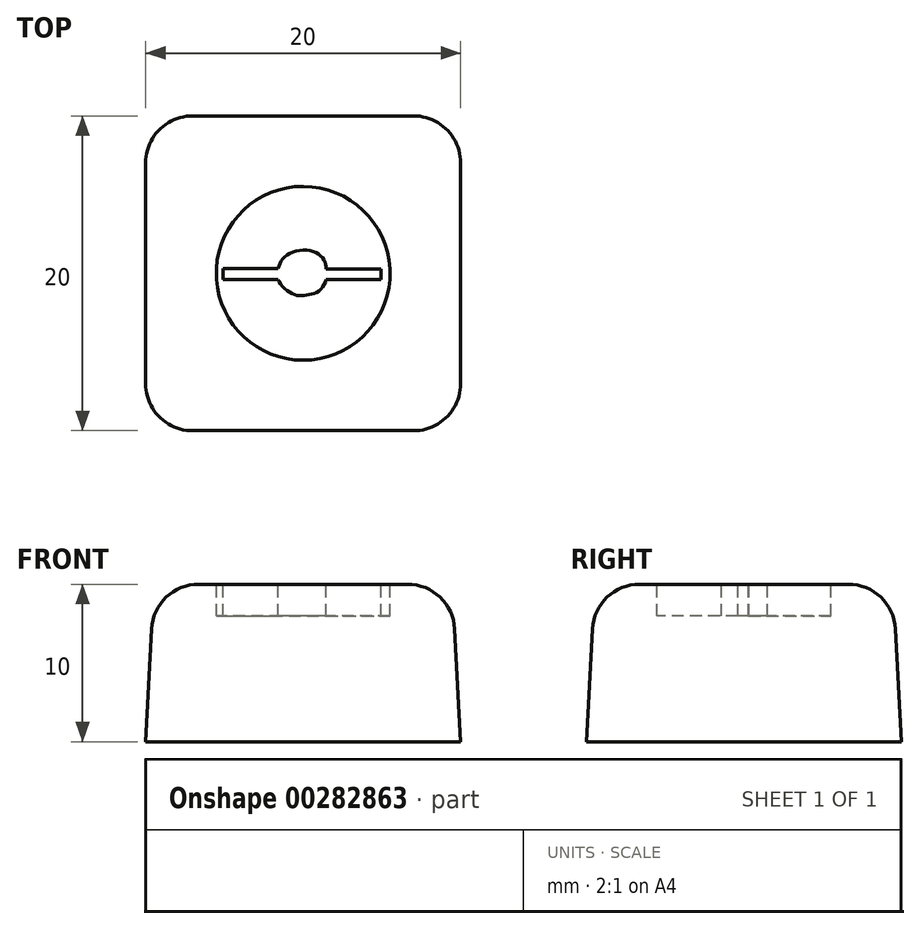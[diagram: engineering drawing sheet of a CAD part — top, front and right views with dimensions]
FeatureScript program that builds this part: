
annotation { "Feature Type Name" : "Feature", "Feature Type Description" : "" }
export const myFeature = defineFeature(function(context is Context, id is Id, definition is map)
    precondition{}
    {
        {
            var Q0;
            Q0=qCreatedBy(makeId("Top.planeOp"),FACE);
            var sketch = newSketch(context, id + "F0", { "sketchPlane" : qUnion([Q0])});
            skLineSegment(sketch, "E0.bottom", {"start": v(10, 10) * mm, "end": v(-10, 10) * mm});
            skLineSegment(sketch, "E0.top", {"start": v(10, -10) * mm, "end": v(-10, -10) * mm});
            skLineSegment(sketch, "E0.left", {"start": v(10, 10) * mm, "end": v(10, -10) * mm});
            skLineSegment(sketch, "E0.right", {"start": v(-10, 10) * mm, "end": v(-10, -10) * mm});
            skPoint(sketch, "E0.middle", {"position": v(0, 0) * mm});
            skSolve(sketch);
        }
        {
            var Q0;
            Q0 = qSketchRegion(id + "F0", true);
            extrude(context, id + "F1", {"entities" : qUnion([Q0]), "depth" : 10 * mm, "hasDraft" : true, "draftAngle" : 3 * degree, "draftPullDirection" : true});
        }
        {
            var Q0;
            Q0=makeQuery(id+"F1.opExtrude","CAP_EDGE",EDGE,{"disambiguationData":[OSD([sQuery(id+"F0.wireOp",EDGE,"E0.bottom")])],"isStart":false});
            var Q1;
            Q1=makeQuery(id+"F1.opExtrude","SWEPT_EDGE",EDGE,{"disambiguationData":[OSD([sQuery(id+"F0.wireOp",EDGE,"E0.bottom"),sQuery(id+"F0.wireOp",EDGE,"E0.left")])]});
            var Q2;
            Q2=makeQuery(id+"F1.opExtrude","CAP_EDGE",EDGE,{"disambiguationData":[OSD([sQuery(id+"F0.wireOp",EDGE,"E0.left")])],"isStart":false});
            var Q3;
            Q3=makeQuery(id+"F1.opExtrude","SWEPT_EDGE",EDGE,{"disambiguationData":[OSD([sQuery(id+"F0.wireOp",EDGE,"E0.top"),sQuery(id+"F0.wireOp",EDGE,"E0.left")])]});
            var Q4;
            Q4=makeQuery(id+"F1.opExtrude","CAP_EDGE",EDGE,{"disambiguationData":[OSD([sQuery(id+"F0.wireOp",EDGE,"E0.top")])],"isStart":false});
            var Q5;
            Q5=makeQuery(id+"F1.opExtrude","CAP_EDGE",EDGE,{"disambiguationData":[OSD([sQuery(id+"F0.wireOp",EDGE,"E0.right")])],"isStart":false});
            var Q6;
            Q6=makeQuery(id+"F1.opExtrude","SWEPT_EDGE",EDGE,{"disambiguationData":[OSD([sQuery(id+"F0.wireOp",EDGE,"E0.top"),sQuery(id+"F0.wireOp",EDGE,"E0.right")])]});
            var Q7;
            Q7=makeQuery(id+"F1.opExtrude","SWEPT_EDGE",EDGE,{"disambiguationData":[OSD([sQuery(id+"F0.wireOp",EDGE,"E0.bottom"),sQuery(id+"F0.wireOp",EDGE,"E0.right")])]});
            fillet(context, id + "F2", {"entities" : qUnion([Q0, Q1, Q2, Q3, Q4, Q5, Q6, Q7]), "radius" : 3 * mm, "tangentPropagation" : true, "allowEdgeOverflow" : false});
        }
        {
            var Q0;
            Q0=makeQuery(id+"F1.opExtrude","CAP_FACE",FACE,{"disambiguationData":[OSD([sQuery(id+"F0.wireOp",EDGE,"E0.bottom"),sQuery(id+"F0.wireOp",EDGE,"E0.top"),sQuery(id+"F0.wireOp",EDGE,"E0.left"),sQuery(id+"F0.wireOp",EDGE,"E0.right")])],"isStart":false});
            var sketch = newSketch(context, id + "F3", { "sketchPlane" : qUnion([Q0])});
            skArc(sketch, "E1", {"start": v(-5.5, -0.38) * mm, "mid": v(0, -5.52) * mm, "end": v(5.5, -0.38) * mm});
            skLineSegment(sketch, "E2", {"start": v(-5.51, 0.31) * mm, "end": v(-1.58, 0.31) * mm});
            skLineSegment(sketch, "E3", {"start": v(1.46, 0.29) * mm, "end": v(5.51, 0.29) * mm});
            skLineSegment(sketch, "E4", {"start": v(-5.5, -0.38) * mm, "end": v(-1.58, -0.38) * mm});
            skLineSegment(sketch, "E5", {"start": v(1.46, -0.38) * mm, "end": v(5.5, -0.38) * mm});
            skFitSpline(sketch, "E6", {"points": [v(-1.58, 0.31) * mm, v(-1.12, 1.09) * mm, v(0.27, 1.47) * mm, v(1.25, 0.96) * mm, v(1.46, 0.29) * mm, v(1.46, -0.38) * mm, v(1.02, -1.1) * mm, v(0.33, -1.37) * mm, v(-0.3, -1.42) * mm, v(-1.04, -1.08) * mm, v(-1.58, -0.38) * mm, v(-1.58, 0.31) * mm]});
            skArc(sketch, "E7.trimOffspring", {"start": v(5.51, 0.29) * mm, "mid": v(0.01, 5.52) * mm, "end": v(-5.51, 0.31) * mm});
            skLineSegment(sketch, "E8", {"start": v(-5.51, 0.31) * mm, "end": v(-5.5, -0.38) * mm});
            skLineSegment(sketch, "E9", {"start": v(5.51, 0.29) * mm, "end": v(5.5, -0.38) * mm});
            skLineSegment(sketch, "E10", {"start": v(-5.1, 0.31) * mm, "end": v(-5.1, -0.38) * mm});
            skLineSegment(sketch, "E11", {"start": v(4.94, 0.29) * mm, "end": v(4.94, -0.38) * mm});
            skSolve(sketch);
        }
        {
            var Q0;
            {var subQ0=sQuery(id+"F3.wireOp",EDGE,"E2");Q0=makeQuery(id+"F3.imprint","IMPRINT",FACE,{"disambiguationData":[TD([[makeQuery(id+"F3.imprint","IMPRINT",EDGE,{"derivedFrom":subQ0}),1.0]])]});}
            var Q1;
            {var subQ0=sQuery(id+"F3.wireOp",EDGE,"E4");Q1=makeQuery(id+"F3.imprint","IMPRINT",FACE,{"disambiguationData":[TD([[makeQuery(id+"F3.imprint","IMPRINT",EDGE,{"derivedFrom":subQ0}),-1.0]])]});}
            var Q2;
            {var subQ0=sQuery(id+"F3.wireOp",EDGE,"E8");Q2=makeQuery(id+"F3.imprint","IMPRINT",FACE,{"disambiguationData":[TD([[makeQuery(id+"F3.imprint","IMPRINT",EDGE,{"derivedFrom":subQ0}),1.0]])]});}
            var Q3;
            {var subQ0=sQuery(id+"F3.wireOp",EDGE,"E9");Q3=makeQuery(id+"F3.imprint","IMPRINT",FACE,{"disambiguationData":[TD([[makeQuery(id+"F3.imprint","IMPRINT",EDGE,{"derivedFrom":subQ0}),-1.0]])]});}
            extrude(context, id + "F4", {"entities" : qUnion([Q0, Q1, Q2, Q3]), "operationType" : NewBodyOperationType.REMOVE, "oppositeDirection" : true, "depth" : 2 * mm});
        }
    });
